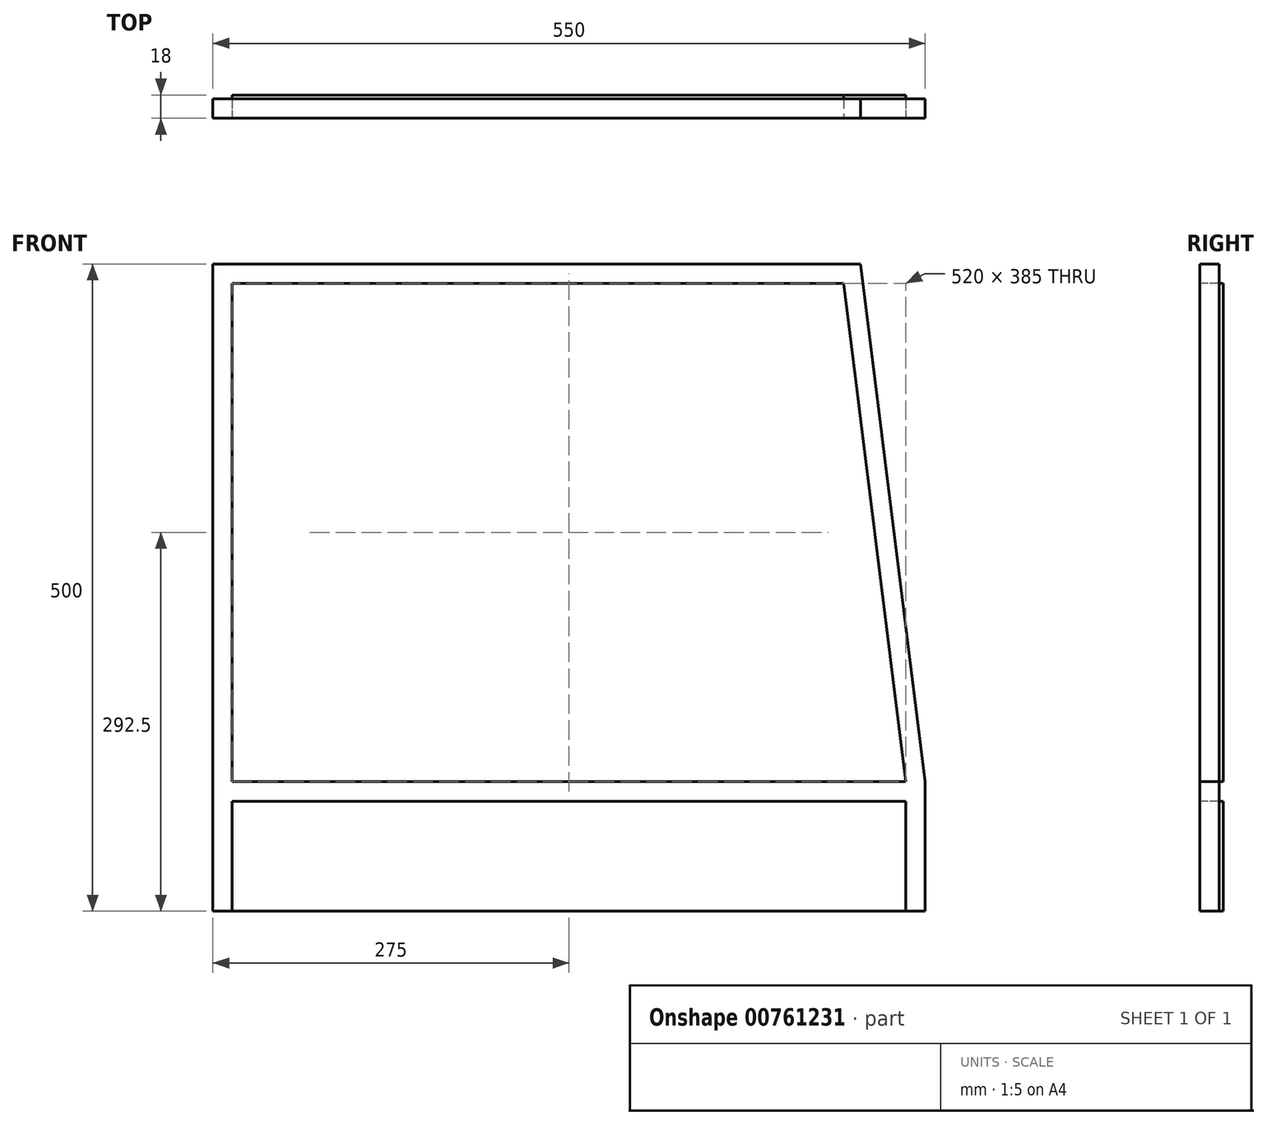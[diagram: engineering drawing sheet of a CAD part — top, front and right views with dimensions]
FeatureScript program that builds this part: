
annotation { "Feature Type Name" : "Feature", "Feature Type Description" : "" }
export const myFeature = defineFeature(function(context is Context, id is Id, definition is map)
    precondition{}
    {
        {
            var Q0;
            Q0=qCreatedBy(makeId("Front.planeOp"),FACE);
            var sketch = newSketch(context, id + "F0", { "sketchPlane" : qUnion([Q0])});
            skLineSegment(sketch, "E0.bottom", {"start": v(225, 250) * mm, "end": v(-275, 250) * mm});
            skLineSegment(sketch, "E0.top", {"start": v(275, -250) * mm, "end": v(-275, -250) * mm});
            skLineSegment(sketch, "E0.left", {"start": v(275, -150) * mm, "end": v(275, -250) * mm});
            skLineSegment(sketch, "E0.right", {"start": v(-275, 250) * mm, "end": v(-275, -250) * mm});
            skPoint(sketch, "E0.middle", {"position": v(0, 0) * mm});
            skLineSegment(sketch, "E1", {"start": v(275, -150) * mm, "end": v(225, 250) * mm});
            skPoint(sketch, "E2.orphan", {"position": v(275, 250) * mm});
            skLineSegment(sketch, "E3", {"start": v(260, -150) * mm, "end": v(-260, -150) * mm});
            skLineSegment(sketch, "E4", {"start": v(-260, -165) * mm, "end": v(260, -165) * mm});
            skLineSegment(sketch, "E5", {"start": v(-260, 235) * mm, "end": v(-260, -150) * mm});
            skLineSegment(sketch, "E6", {"start": v(260, -250) * mm, "end": v(260, -165) * mm});
            skLineSegment(sketch, "E7", {"start": v(260, -150) * mm, "end": v(211.87, 235) * mm});
            skLineSegment(sketch, "E8", {"start": v(-260, 235) * mm, "end": v(211.87, 235) * mm});
            skPoint(sketch, "E9.orphan", {"position": v(-275, 235) * mm});
            skPoint(sketch, "E10.orphan", {"position": v(-260, 250) * mm});
            skPoint(sketch, "E11.orphan", {"position": v(225, 235) * mm});
            skPoint(sketch, "E12.orphan", {"position": v(-275, -165) * mm});
            skPoint(sketch, "E13.orphan", {"position": v(-275, -150) * mm});
            skLineSegment(sketch, "E14.trimOffspring", {"start": v(-260, -165) * mm, "end": v(-260, -250) * mm});
            skSolve(sketch);
        }
        {
            var Q0;
            Q0=makeQuery(id+"F0.imprint","IMPRINT",FACE,{"disambiguationData":[TD([[makeQuery(id+"F0.imprint","IMPRINT",EDGE,{"derivedFrom":sQuery(id+"F0.wireOp",EDGE,"E3")}),-1.0]])]});
            var Q1;
            Q1=makeQuery(id+"F0.imprint","IMPRINT",FACE,{"disambiguationData":[TD([[makeQuery(id+"F0.imprint","IMPRINT",EDGE,{"derivedFrom":sQuery(id+"F0.wireOp",EDGE,"E4")}),-1.0]])]});
            extrude(context, id + "F1", {"entities" : qUnion([Q0, Q1]), "oppositeDirection" : true, "depth" : 18 * mm, "offsetDistance" : 25 * mm});
        }
        {
            var Q0;
            Q0=makeQuery(id+"F0.imprint","IMPRINT",FACE,{"disambiguationData":[TD([[makeQuery(id+"F0.imprint","IMPRINT",EDGE,{"derivedFrom":sQuery(id+"F0.wireOp",EDGE,"E0.bottom")}),1.0]])]});
            extrude(context, id + "F2", {"entities" : qUnion([Q0]), "oppositeDirection" : true, "depth" : 15 * mm, "offsetDistance" : 25 * mm});
        }
    });
